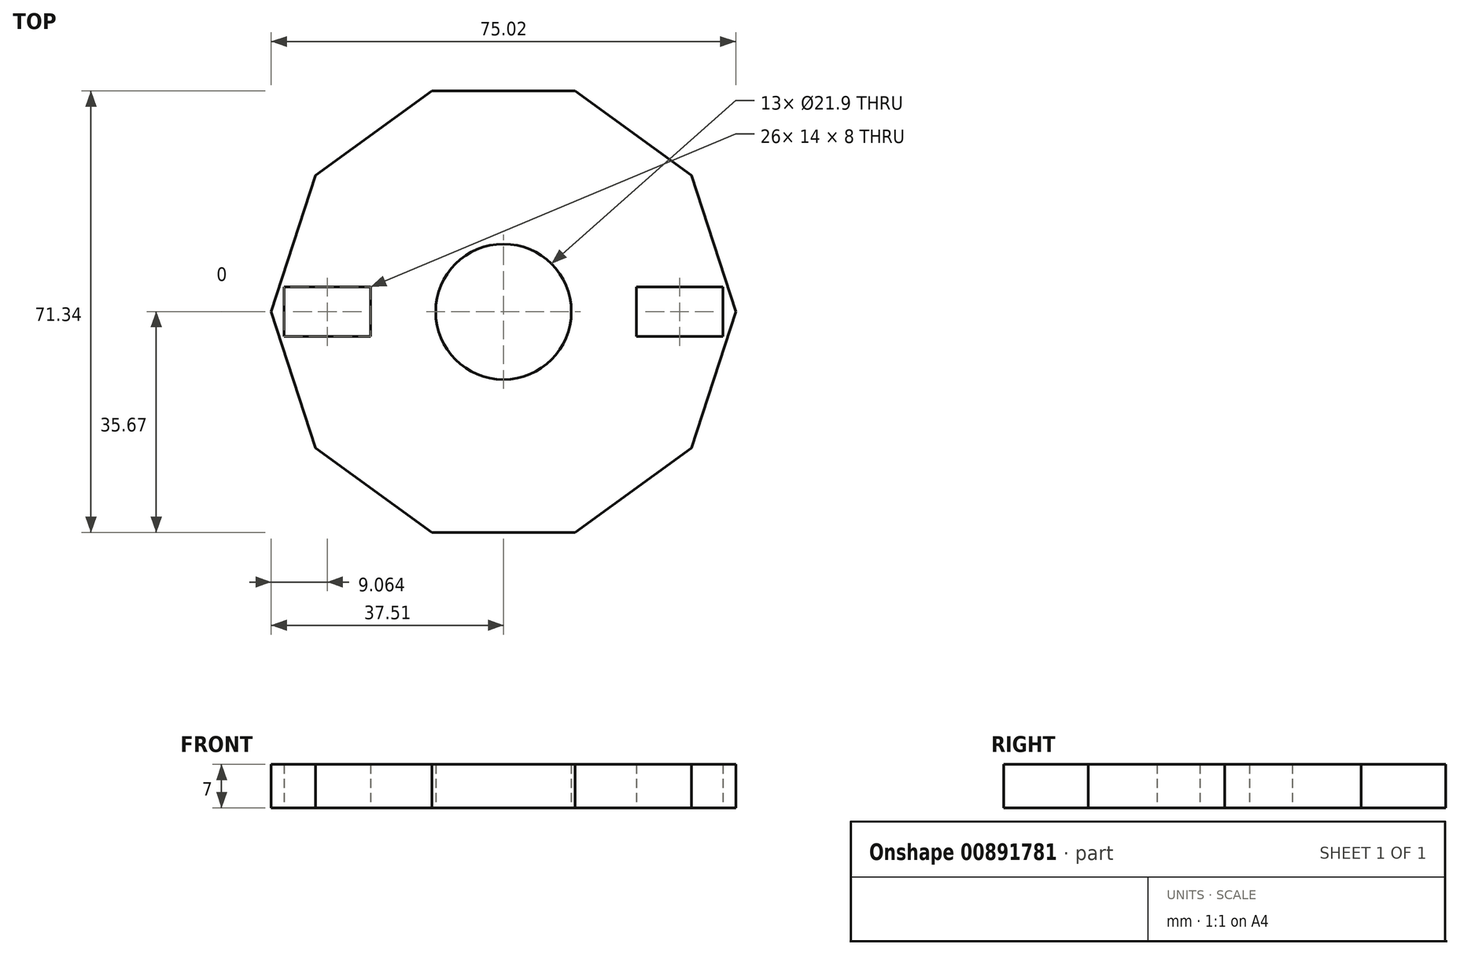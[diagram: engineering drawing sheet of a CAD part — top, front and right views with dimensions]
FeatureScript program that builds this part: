
annotation { "Feature Type Name" : "Feature", "Feature Type Description" : "" }
export const myFeature = defineFeature(function(context is Context, id is Id, definition is map)
    precondition{}
    {
        {
            var Q0;
            Q0=qCreatedBy(makeId("Top.planeOp"),FACE);
            var sketch = newSketch(context, id + "F0", { "sketchPlane" : qUnion([Q0])});
            skCircle(sketch, "E0.cCircle", {"center": v(0, 0) * mm, "radius": 35.67 * mm, "construction": true});
            skLineSegment(sketch, "E0.0", {"start": v(-11.6, 35.67) * mm, "end": v(11.6, 35.67) * mm});
            skLineSegment(sketch, "E0.1", {"start": v(11.6, 35.67) * mm, "end": v(30.34, 22.05) * mm});
            skLineSegment(sketch, "E0.2", {"start": v(30.34, 22.05) * mm, "end": v(37.5, 0) * mm});
            skLineSegment(sketch, "E0.3", {"start": v(37.5, 0) * mm, "end": v(30.34, -22.05) * mm});
            skLineSegment(sketch, "E0.4", {"start": v(30.34, -22.05) * mm, "end": v(11.6, -35.67) * mm});
            skLineSegment(sketch, "E0.5", {"start": v(11.6, -35.67) * mm, "end": v(-11.6, -35.67) * mm});
            skLineSegment(sketch, "E0.6", {"start": v(-11.6, -35.67) * mm, "end": v(-30.34, -22.05) * mm});
            skLineSegment(sketch, "E0.7", {"start": v(-30.34, -22.05) * mm, "end": v(-37.5, 0) * mm});
            skLineSegment(sketch, "E0.8", {"start": v(-37.5, 0) * mm, "end": v(-30.34, 22.05) * mm});
            skLineSegment(sketch, "E0.9", {"start": v(-30.34, 22.05) * mm, "end": v(-11.6, 35.67) * mm});
            skPoint(sketch, "E0.0.midPoint", {"position": v(0, 35.67) * mm});
            skCircle(sketch, "E1", {"center": v(0, 0) * mm, "radius": 10.95 * mm});
            skLineSegment(sketch, "E2.bottom", {"start": v(35.45, 4) * mm, "end": v(21.45, 4) * mm});
            skLineSegment(sketch, "E2.top", {"start": v(35.45, -4) * mm, "end": v(21.45, -4) * mm});
            skLineSegment(sketch, "E2.left", {"start": v(35.45, 4) * mm, "end": v(35.45, -4) * mm});
            skLineSegment(sketch, "E2.right", {"start": v(21.45, 4) * mm, "end": v(21.45, -4) * mm});
            skPoint(sketch, "E2.middle", {"position": v(28.45, 0) * mm});
            skLineSegment(sketch, "E3.bottom", {"start": v(-35.45, 4) * mm, "end": v(-21.45, 4) * mm});
            skLineSegment(sketch, "E3.top", {"start": v(-35.45, -4) * mm, "end": v(-21.45, -4) * mm});
            skLineSegment(sketch, "E3.left", {"start": v(-35.45, 4) * mm, "end": v(-35.45, -4) * mm});
            skLineSegment(sketch, "E3.right", {"start": v(-21.45, 4) * mm, "end": v(-21.45, -4) * mm});
            skPoint(sketch, "E3.middle", {"position": v(-28.45, 0) * mm});
            skSolve(sketch);
        }
        {
            var Q0;
            Q0=makeQuery(id+"F0.imprint","IMPRINT",FACE,{"disambiguationData":[TD([[makeQuery(id+"F0.imprint","IMPRINT",EDGE,{"derivedFrom":sQuery(id+"F0.wireOp",EDGE,"E0.0")}),-1.0]])]});
            extrude(context, id + "F1", {"entities" : qUnion([Q0]), "depth" : 7 * mm, "offsetDistance" : 25 * mm});
        }
    });
